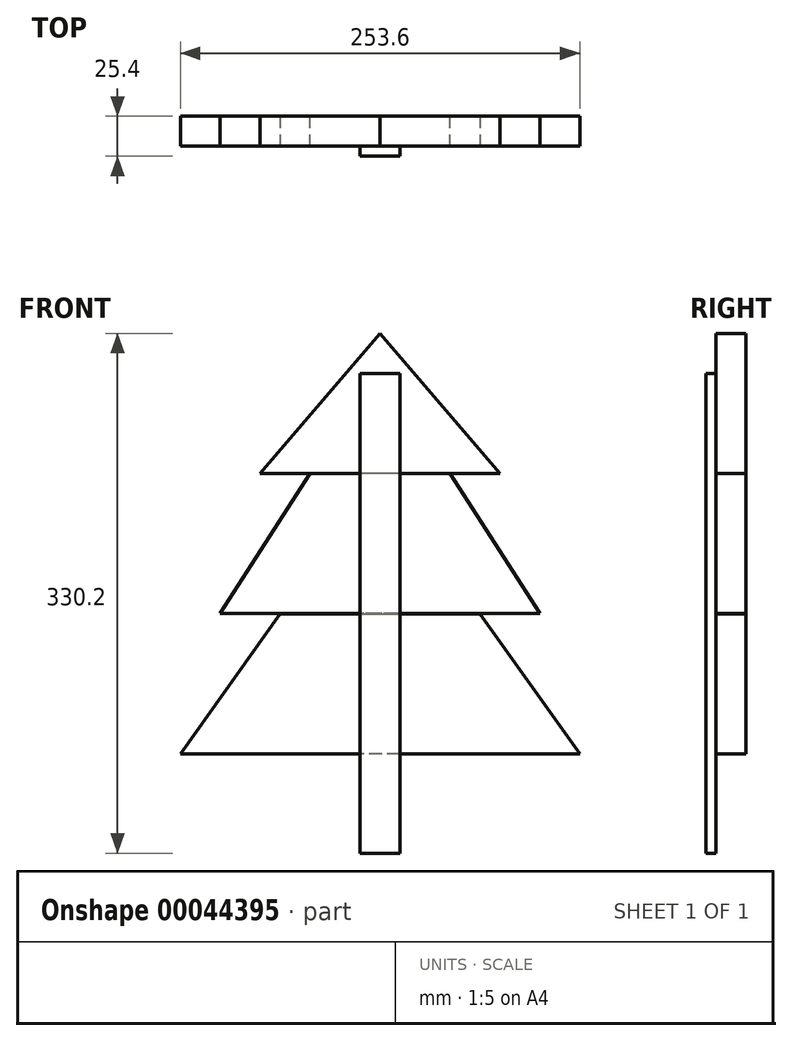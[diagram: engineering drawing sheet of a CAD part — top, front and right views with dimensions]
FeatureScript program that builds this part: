
annotation { "Feature Type Name" : "Feature", "Feature Type Description" : "" }
export const myFeature = defineFeature(function(context is Context, id is Id, definition is map)
    precondition{}
    {
        {
            var Q0;
            Q0=qCreatedBy(makeId("Front.planeOp"),FACE);
            var sketch = newSketch(context, id + "F0", { "sketchPlane" : qUnion([Q0])});
            skLineSegment(sketch, "E0", {"start": v(0, 0) * mm, "end": v(-76.2, 0) * mm});
            skLineSegment(sketch, "E1", {"start": v(-76.2, 0) * mm, "end": v(0, 88.9) * mm});
            skLineSegment(sketch, "E2.MirrorCS", {"start": v(76.2, 0) * mm, "end": v(0, 88.9) * mm});
            skLineSegment(sketch, "E3.MirrorCS", {"start": v(0, 0) * mm, "end": v(76.2, 0) * mm});
            skSolve(sketch);
        }
        {
            var Q0;
            Q0 = qSketchRegion(id + "F0", true);
            extrude(context, id + "F1", {"entities" : qUnion([Q0]), "oppositeDirection" : true, "depth" : 19.05 * mm});
        }
        {
            var Q0;
            Q0=makeQuery(id+"F1.opExtrude","CAP_FACE",FACE,{"disambiguationData":[OSD([sQuery(id+"F0.wireOp",EDGE,"E0"),sQuery(id+"F0.wireOp",EDGE,"E1"),sQuery(id+"F0.wireOp",EDGE,"E2.MirrorCS"),sQuery(id+"F0.wireOp",EDGE,"E3.MirrorCS")])],"isStart":false});
            var sketch = newSketch(context, id + "F2", { "sketchPlane" : qUnion([Q0])});
            skLineSegment(sketch, "E4", {"start": v(-44.45, 0) * mm, "end": v(-101.6, -88.9) * mm});
            skLineSegment(sketch, "E5", {"start": v(-101.6, -88.9) * mm, "end": v(0, -88.9) * mm});
            skLineSegment(sketch, "E6.MirrorCS", {"start": v(44.45, 0) * mm, "end": v(101.6, -88.9) * mm});
            skLineSegment(sketch, "E7.MirrorCS", {"start": v(101.6, -88.9) * mm, "end": v(0, -88.9) * mm});
            skLineSegment(sketch, "E8", {"start": v(-44.45, 0) * mm, "end": v(44.45, 0) * mm});
            skSolve(sketch);
        }
        {
            var Q0;
            {var subQ2=sQuery(id+"F2.wireOp",EDGE,"E4");Q0=makeQuery(id+"F2.imprint","IMPRINT",FACE,{"disambiguationData":[TD([[makeQuery(id+"F2.imprint","IMPRINT",EDGE,{"derivedFrom":subQ2}),1.0]])]});}
            extrude(context, id + "F3", {"entities" : qUnion([Q0]), "oppositeDirection" : true, "depth" : 19.05 * mm});
        }
        {
            var Q0;
            Q0=qCreatedBy(makeId("Front.planeOp"),FACE);
            var sketch = newSketch(context, id + "F4", { "sketchPlane" : qUnion([Q0])});
            skLineSegment(sketch, "E9", {"start": v(-63.5, -89.17) * mm, "end": v(63.5, -89.17) * mm});
            skLineSegment(sketch, "E10.MirrorCS", {"start": v(-63.5, -89.17) * mm, "end": v(-127, -178.35) * mm});
            skLineSegment(sketch, "E11.MirrorCS", {"start": v(0, -178.07) * mm, "end": v(-127, -178.07) * mm});
            skLineSegment(sketch, "E12.MirrorCS", {"start": v(0, -178.07) * mm, "end": v(127, -178.07) * mm});
            skLineSegment(sketch, "E13.MirrorCS", {"start": v(63.5, -89.17) * mm, "end": v(127, -178.35) * mm});
            skSolve(sketch);
        }
        {
            var Q0;
            Q0 = qSketchRegion(id + "F4", true);
            extrude(context, id + "F5", {"entities" : qUnion([Q0]), "oppositeDirection" : true, "depth" : 19.05 * mm});
        }
        {
            var Q0;
            Q0=qCreatedBy(makeId("Front.planeOp"),FACE);
            var sketch = newSketch(context, id + "F6", { "sketchPlane" : qUnion([Q0])});
            skLineSegment(sketch, "E14", {"start": v(0, 63.5) * mm, "end": v(-12.7, 63.5) * mm});
            skLineSegment(sketch, "E15", {"start": v(-12.7, 63.5) * mm, "end": v(-12.7, -241.3) * mm});
            skLineSegment(sketch, "E16", {"start": v(-12.7, -241.3) * mm, "end": v(0, -241.3) * mm});
            skLineSegment(sketch, "E17.MirrorCS", {"start": v(12.7, -241.3) * mm, "end": v(0, -241.3) * mm});
            skLineSegment(sketch, "E18.MirrorCS", {"start": v(12.7, 63.5) * mm, "end": v(12.7, -241.3) * mm});
            skLineSegment(sketch, "E19.MirrorCS", {"start": v(0, 63.5) * mm, "end": v(12.7, 63.5) * mm});
            skSolve(sketch);
        }
        {
            var Q0;
            Q0 = qSketchRegion(id + "F6", true);
            extrude(context, id + "F7", {"entities" : qUnion([Q0]), "depth" : 6.35 * mm});
        }
    });
